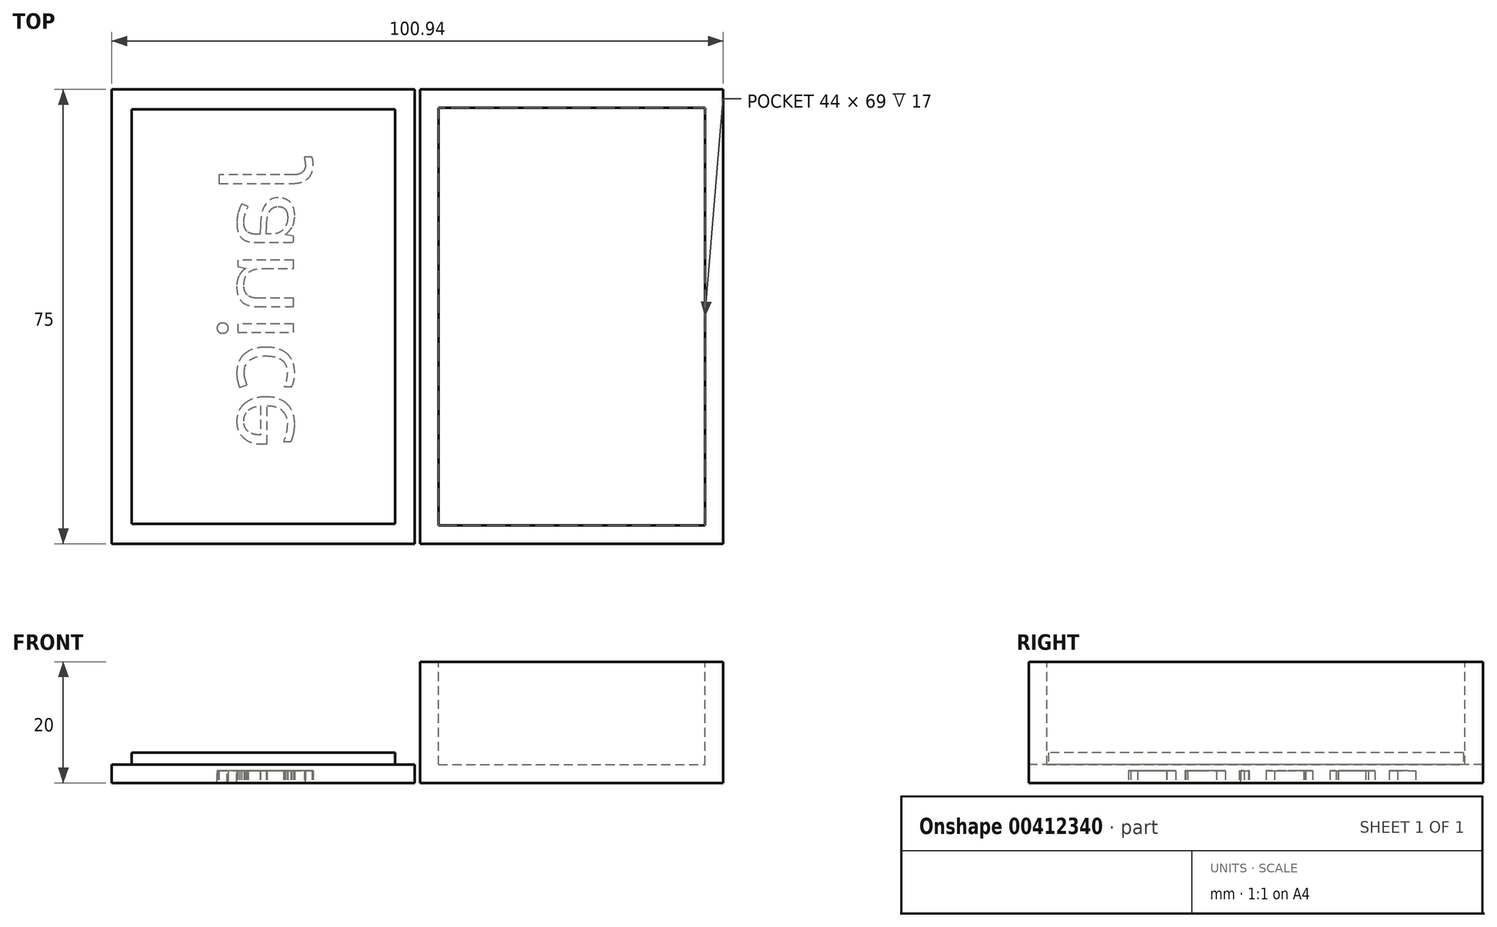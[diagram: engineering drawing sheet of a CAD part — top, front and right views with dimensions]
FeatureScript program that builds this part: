
annotation { "Feature Type Name" : "Feature", "Feature Type Description" : "" }
export const myFeature = defineFeature(function(context is Context, id is Id, definition is map)
    precondition{}
    {
        {
            var Q0;
            Q0=qCreatedBy(makeId("Top.planeOp"),FACE);
            var sketch = newSketch(context, id + "F0", { "sketchPlane" : qUnion([Q0])});
            skLineSegment(sketch, "E0.bottom", {"start": v(0, 0) * mm, "end": v(50, 0) * mm});
            skLineSegment(sketch, "E0.top", {"start": v(0, 75) * mm, "end": v(50, 75) * mm});
            skLineSegment(sketch, "E0.left", {"start": v(0, 0) * mm, "end": v(0, 75) * mm});
            skLineSegment(sketch, "E0.right", {"start": v(50, 0) * mm, "end": v(50, 75) * mm});
            skSolve(sketch);
        }
        {
            var Q0;
            Q0=makeQuery(id+"F0.imprint","IMPRINT",FACE,{"disambiguationData":[TD([[makeQuery(id+"F0.imprint","IMPRINT",EDGE,{"derivedFrom":sQuery(id+"F0.wireOp",EDGE,"E0.bottom")}),1.0]])]});
            extrude(context, id + "F1", {"entities" : qUnion([Q0]), "depth" : 20 * mm});
        }
        {
            var Q0;
            Q0=makeQuery(id+"F1.opExtrude","CAP_FACE",FACE,{"disambiguationData":[OSD([sQuery(id+"F0.wireOp",EDGE,"E0.bottom"),sQuery(id+"F0.wireOp",EDGE,"E0.top"),sQuery(id+"F0.wireOp",EDGE,"E0.left"),sQuery(id+"F0.wireOp",EDGE,"E0.right")])],"isStart":false});
            var sketch = newSketch(context, id + "F2", { "sketchPlane" : qUnion([Q0])});
            skLineSegment(sketch, "E1.bottom", {"start": v(3, 3) * mm, "end": v(47, 3) * mm});
            skLineSegment(sketch, "E1.top", {"start": v(3, 72) * mm, "end": v(47, 72) * mm});
            skLineSegment(sketch, "E1.left", {"start": v(3, 3) * mm, "end": v(3, 72) * mm});
            skLineSegment(sketch, "E1.right", {"start": v(47, 3) * mm, "end": v(47, 72) * mm});
            skSolve(sketch);
        }
        {
            var Q0;
            Q0=makeQuery(id+"F2.imprint","IMPRINT",FACE,{"disambiguationData":[TD([[makeQuery(id+"F2.imprint","IMPRINT",EDGE,{"derivedFrom":sQuery(id+"F2.wireOp",EDGE,"E1.bottom")}),1.0]])]});
            extrude(context, id + "F3", {"entities" : qUnion([Q0]), "operationType" : NewBodyOperationType.REMOVE, "oppositeDirection" : true, "depth" : 17 * mm});
        }
        {
            var Q0;
            Q0=qCreatedBy(makeId("Top.planeOp"),FACE);
            var sketch = newSketch(context, id + "F4", { "sketchPlane" : qUnion([Q0])});
            skLineSegment(sketch, "E2.bottom", {"start": v(-50.94, 75) * mm, "end": v(-0.94, 75) * mm});
            skLineSegment(sketch, "E2.top", {"start": v(-50.94, 0) * mm, "end": v(-0.94, 0) * mm});
            skLineSegment(sketch, "E2.left", {"start": v(-50.94, 75) * mm, "end": v(-50.94, 0) * mm});
            skLineSegment(sketch, "E2.right", {"start": v(-0.94, 75) * mm, "end": v(-0.94, 0) * mm});
            skSolve(sketch);
        }
        {
            var Q0;
            Q0=makeQuery(id+"F4.imprint","IMPRINT",FACE,{"disambiguationData":[TD([[makeQuery(id+"F4.imprint","IMPRINT",EDGE,{"derivedFrom":sQuery(id+"F4.wireOp",EDGE,"E2.bottom")}),-1.0]])]});
            extrude(context, id + "F5", {"entities" : qUnion([Q0]), "depth" : 3 * mm});
        }
        {
            var Q0;
            Q0=makeQuery(id+"F5.opExtrude","CAP_FACE",FACE,{"disambiguationData":[OSD([sQuery(id+"F4.wireOp",EDGE,"E2.bottom"),sQuery(id+"F4.wireOp",EDGE,"E2.top"),sQuery(id+"F4.wireOp",EDGE,"E2.left"),sQuery(id+"F4.wireOp",EDGE,"E2.right")])],"isStart":false});
            var sketch = newSketch(context, id + "F6", { "sketchPlane" : qUnion([Q0])});
            skLineSegment(sketch, "E3.bottom", {"start": v(-47.69, 71.75) * mm, "end": v(-4.19, 71.75) * mm});
            skLineSegment(sketch, "E3.top", {"start": v(-47.69, 3.25) * mm, "end": v(-4.19, 3.25) * mm});
            skLineSegment(sketch, "E3.left", {"start": v(-47.69, 71.75) * mm, "end": v(-47.69, 3.25) * mm});
            skLineSegment(sketch, "E3.right", {"start": v(-4.19, 71.75) * mm, "end": v(-4.19, 3.25) * mm});
            skSolve(sketch);
        }
        {
            var Q0;
            Q0=makeQuery(id+"F6.imprint","IMPRINT",FACE,{"disambiguationData":[TD([[makeQuery(id+"F6.imprint","IMPRINT",EDGE,{"derivedFrom":sQuery(id+"F6.wireOp",EDGE,"E3.bottom")}),-1.0]])]});
            extrude(context, id + "F7", {"entities" : qUnion([Q0]), "operationType" : NewBodyOperationType.ADD, "depth" : 2 * mm});
        }
        {
            var Q0;
            Q0=makeQuery(id+"F5.opExtrude","CAP_FACE",FACE,{"disambiguationData":[OSD([sQuery(id+"F4.wireOp",EDGE,"E2.bottom"),sQuery(id+"F4.wireOp",EDGE,"E2.top"),sQuery(id+"F4.wireOp",EDGE,"E2.left"),sQuery(id+"F4.wireOp",EDGE,"E2.right")])],"isStart":true});
            var sketch = newSketch(context, id + "F8", { "sketchPlane" : qUnion([Q0])});
            skText(sketch, "E4", { "text": "Janice\n", "fontName": "OpenSans-Regular.ttf"});
            const initialGuessF8  = {"E4": [-0.02092, -0.06252, 0, 1, 0.0124]};
            skSetInitialGuess(sketch, initialGuessF8);
            skSolve(sketch);
        }
        {
            var Q0;
            Q0 = qSketchRegion(id + "F8", true);
            extrude(context, id + "F9", {"entities" : qUnion([Q0]), "operationType" : NewBodyOperationType.REMOVE, "oppositeDirection" : true, "depth" : 2 * mm});
        }
    });
